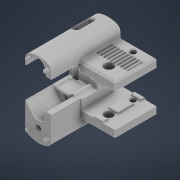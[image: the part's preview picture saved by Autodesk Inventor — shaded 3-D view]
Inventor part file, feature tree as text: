
AUTODESK INVENTOR PART (.ipt)
format: ipt  version: 2022.1 (Build 261234000, 234)  size: 1,613,312 bytes
history: native  units: mm
features: projected_geometry x40, extrude x31, sketch x31, reference x20, chamfer x19, other x11, move_body x11, direct_edit x8, fillet x7, hole x5, delete_face x5, plane x4, mirror x1
ambient origin geometry x8: Origin, YZ Plane, XZ Plane, XY Plane, X Axis, Y Axis, Z Axis, Center Point
bodies: Volumenkörper1 (feature_tree)
feature tree (193):
  extrude  "Extrusion1"  Depth=20.0mm
  extrude  "Extrusion2"  Depth=25.0mm
  plane  "Arbeitsebene1"
  extrude  "Extrusion5"  Depth=20.0mm
  sketch  "Skizze5"  dims[d7=20.0mm d8=10.0mm]
  extrude  "Extrusion6"  Depth=10.0mm
  hole  "Bohrung1"  [1 undecoded]
  extrude  "Extrusion10"  Depth=7.1mm
  sketch  "Skizze10"  dims[d28=15.0mm d29=17.0mm]
  hole  "Bohrung2"  [1 undecoded]
  hole  "Bohrung3"  [1 undecoded]
  extrude  "Extrusion11"  Depth=0.1mm
  extrude  "Extrusion12"  Depth=7.1mm
  direct_edit  "Direktbearbeitung3"
  direct_edit  "Direktbearbeitung4"
  extrude  "Extrusion13"  Depth=7.1mm
  fillet  "Rundung6"  Radius=18.2mm
  direct_edit  "Direktbearbeitung5"
  extrude  "Extrusion14"  Depth=11.0mm TaperAngle=0.0deg
  chamfer  "Fase2"  [1 undecoded]
  chamfer  "Fase3"  [1 undecoded]
  hole  "Bohrung5"  [1 undecoded]
  extrude  "Extrusion18"  Depth=4.0mm TaperAngle=0.0deg
  chamfer  "Fase4"  Distance=11.0mm
  extrude  "Extrusion19"  TaperAngle=0.0deg  [1 undecoded]
  chamfer  "Fase5"  Distance=1.2mm
  plane  "Arbeitsebene2"
  mirror  "Spiegeln1"
  extrude  "Extrusion20"  Depth=0.6mm
  fillet  "Rundung7"  Radius=1.2mm
  extrude  "Extrusion21"  Depth=0.6mm
  chamfer  "Fase6"  Distance=1.2mm
  extrude  "Extrusion22"  Depth=0.6mm
  chamfer  "Fase7"  Distance=6.2mm
  fillet  "Rundung8"  Radius=2.269mm
  chamfer  "Fase8"  Distance=10.561825mm
  chamfer  "Fase9"  Distance=10.561825mm
  extrude  "Extrusion23"  Depth=0.6mm
  extrude  "Extrusion24"  Depth=0.6mm
  direct_edit  "Direktbearbeitung6"
  direct_edit  "Direktbearbeitung7"
  chamfer  "Fase10"  Distance=0.8mm
  chamfer  "Fase11"  Distance=0.8mm
  fillet  "Rundung11"  Radius=0.8mm
  sketch  "Skizze27"  dims[d66=5.2mm d67=6.0mm d68=4.0mm d69=2.0mm d70=90.0deg d71=8.0mm d72=0.0mm]
  extrude  "Extrusion25"  Depth=0.6mm
  extrude  "Extrusion26"  Depth=0.6mm
  plane  "Arbeitsebene4"
  hole  "Bohrung6"  [1 undecoded]
  chamfer  "Fase12"  Distance=0.8mm
  direct_edit  "Direktbearbeitung8"
  plane  "Arbeitsebene3"
  extrude  "Extrusion27"  Depth=0.6mm
  extrude  "Extrusion28"  Depth=0.6mm
  chamfer  "Fase14"  Distance=8.638175mm
  chamfer  "Fase15"  Angle=90.0deg  [1 undecoded]
  chamfer  "Fase16"  Distance=1.0mm
  extrude  "Extrusion29"  Depth=1.0mm TaperAngle=45.0deg
  delete_face  "Fläche löschen1"
  extrude  "Extrusion30"  Depth=1.0mm TaperAngle=45.0deg
  fillet  "Rundung15"  Radius=3.95mm
  extrude  "Extrusion31"  Depth=0.6mm
  delete_face  "Fläche löschen2"
  extrude  "Extrusion32"  Depth=7.1mm
  fillet  "Rundung18"  Radius=1.975mm
  chamfer  "Fase19"  Distance=2.225mm
  chamfer  "Fase20"  [1 undecoded]
  sketch  "Skizze36"  dims[d110=1.2mm]
  extrude  "Extrusion33"  Depth=0.6mm
  extrude  "Extrusion34"  Depth=0.6mm
  extrude  "Extrusion35"  Depth=0.6mm
  delete_face  "Fläche löschen3"
  chamfer  "Fase23"  Distance=2.8mm
  chamfer  "Fase24"  Distance=2.2mm
  direct_edit  "Direktbearbeitung11"
  direct_edit  "Direktbearbeitung12"
  extrude  "Extrusion36"  Depth=0.6mm
  fillet  "Rundung20"  Radius=3.6mm
  sketch  "Skizze39"  dims[d112=1.2mm]
  delete_face  "Fläche löschen4"
  extrude  "Extrusion37"  Depth=0.6mm
  delete_face  "Fläche löschen5"
  extrude  "Extrusion38"  Depth=0.6mm
  chamfer  "Fase25"  Distance=4.95mm
  extrude  "Extrusion39"  Depth=0.5mm TaperAngle=45.0deg
  sketch  "Skizze1"  dims[d0=20.0mm d1=20.0mm]
  sketch  "Skizze2"  dims[d2=21.0mm d3=25.0mm]
  sketch  "Skizze4"  dims[d4=40.0mm d5=0.0mm d6=20.0mm]
  reference  "Referenz2"
  reference  "Referenz3"
  reference  "Referenz4"
  reference  "Referenz5"
  projected_geometry  "Projizierte Kontur2"
  sketch  "Skizze6"  dims[d9=0.0mm d10=0.0mm d11=-5.0mm]
  projected_geometry  "Projizierte Kontur3"
  sketch  "Skizze8"  dims[d25=7.1mm d26=7.1mm]
  reference  "Referenz6"
  reference  "Referenz7"
  projected_geometry  "Projizierte Kontur6"
  projected_geometry  "Projizierte Kontur7"
  reference  "Referenz9"
  sketch  "Skizze11"  dims[d30=1.0mm d31=18.0mm]
  projected_geometry  "Projizierte Kontur8"
  projected_geometry  "Projizierte Kontur9"
  sketch  "Skizze12"  dims[d32=18.2mm d33=0.1mm]
  projected_geometry  "Projizierte Kontur10"
  projected_geometry  "Projizierte Kontur11"
  sketch  "Skizze13"  dims[d34=36.0mm d35=0.0mm d36=7.1mm]
  projected_geometry  "Projizierte Kontur12"
  sketch  "Skizze14"  dims[d37=3.55mm d39=7.1mm d40=18.2mm]
  projected_geometry  "Projizierte Kontur13"
  projected_geometry  "Projizierte Kontur17"
  projected_geometry  "Projizierte Kontur18"
  sketch  "Skizze20"  dims[d41=9.1mm d42=11.0mm d43=0.0mm]
  projected_geometry  "Projizierte Kontur19"
  sketch  "Skizze21"  dims[d48=3.4mm d49=6.0mm d50=4.0mm d51=2.0mm d52=90.0deg d53=8.0mm d54=0.0mm d59=0.0mm d60=0.0mm]
  projected_geometry  "Projizierte Kontur20"
  sketch  "Skizze22"  dims[d61=40.0mm]
  projected_geometry  "Projizierte Kontur21"
  sketch  "Skizze23"  dims[d62=15.5mm]
  projected_geometry  "Projizierte Kontur22"
  sketch  "Skizze24"  dims[d63=10.0mm]
  projected_geometry  "Projizierte Kontur23"
  sketch  "Skizze25"  dims[d64=6.2385mm]
  reference  "Referenz12"
  reference  "Referenz13"
  reference  "Referenz14"
  reference  "Referenz15"
  sketch  "Skizze26"  dims[d65=14.53mm]
  projected_geometry  "Projizierte Kontur24"
  projected_geometry  "Projizierte Kontur25"
  projected_geometry  "Projizierte Kontur26"
  projected_geometry  "Projizierte Kontur27"
  projected_geometry  "Projizierte Kontur28"
  sketch  "Skizze28"  dims[d73=3.2mm d74=6.0mm d75=4.0mm d76=2.0mm d77=90.0deg d78=8.0mm d79=0.0mm d80=0.0mm d81=0.0mm]
  sketch  "Skizze29"  dims[d82=11.0mm d83=0.0mm d87=0.0mm d88=0.0mm d89=4.0mm]
  projected_geometry  "Projizierte Kontur29"
  sketch  "Skizze30"  dims[d90=0.0mm d91=0.0mm d92=4.0mm d93=0.0mm d94=0.0mm d95=4.0mm]
  projected_geometry  "Projizierte Kontur30"
  projected_geometry  "Projizierte Kontur31"
  reference  "Referenz18"
  sketch  "Skizze31"  dims[d101=40.0mm]
  projected_geometry  "Projizierte Kontur32"
  projected_geometry  "Projizierte Kontur33"
  projected_geometry  "Projizierte Kontur34"
  sketch  "Skizze32"  dims[d102=20.0mm d103=11.0mm d104=0.0mm]
  projected_geometry  "Projizierte Kontur35"
  sketch  "Skizze33"  dims[d105=4.0mm d106=0.0mm d107=0.0mm d108=-5.0mm]
  projected_geometry  "Projizierte Kontur36"
  projected_geometry  "Projizierte Kontur37"
  sketch  "Skizze34"  dims[d109=9.4mm]
  projected_geometry  "Projizierte Kontur38"
  projected_geometry  "Projizierte Kontur39"
  reference  "Referenz20"
  projected_geometry  "Projizierte Kontur40"
  projected_geometry  "Projizierte Kontur41"
  sketch  "Skizze37"  dims[d111=1.2mm]
  reference  "Referenz21"
  reference  "Referenz22"
  reference  "Referenz23"
  reference  "Referenz24"
  reference  "Referenz25"
  reference  "Referenz26"
  reference  "Referenz27"
  sketch  "Skizze40"  dims[d113=1.2mm]
  projected_geometry  "Projizierte Kontur42"
  projected_geometry  "Projizierte Kontur43"
  projected_geometry  "Projizierte Kontur44"
  projected_geometry  "Projizierte Kontur45"
  projected_geometry  "Projizierte Kontur46"
  sketch  "Skizze41"  dims[d114=1.2mm d115=1.2mm d116=1.2mm d117=1.2mm d118=1.2mm d119=1.2mm d121=6.2mm d122=6.2mm d123=2.269mm d124=10.561825mm d125=10.561825mm d126=0.8mm d127=0.8mm d128=0.8mm d129=0.8mm d130=0.8mm d131=0.8mm d132=0.8mm d133=0.8mm d134=0.8mm d135=14.53mm d136=6.2385mm d137=8.638175mm d138=90.0deg d139=1.0mm d140=0.0mm d141=1.0mm d142=2.0mm d143=45.0deg d146=1.0mm d147=2.0mm d148=45.0deg d160=3.95mm d161=4.45mm d162=7.1mm d163=1.975mm d164=2.225mm d165=0.0mm d166=3.55mm d169=2.8mm d170=2.8mm d171=2.8mm d172=2.2mm d173=2.8mm d174=6.0mm d175=3.05mm d176=2.0mm d177=8.726646mm d178=7.2mm d179=0.0mm d180=2.0mm d181=3.6mm d182=2.0mm d183=3.6mm d184=4.95mm d185=0.0mm d186=0.5mm d187=2.0mm d188=45.0deg d189=5.8mm d190=25.0mm d191=12.5mm d192=0.0mm d193=1.0mm d194=0.0mm d195=1.0mm d196=2.0mm d197=45.0deg d198=5.0mm d199=0.0mm d200=0.0mm d201=1.0mm d202=1.0mm d203=0.0mm d204=1.0mm d205=2.0mm d206=45.0deg d207=135.0deg d208=0.0mm d209=0.0mm d210=1.0mm d211=2.0mm d212=45.0deg d213=5.0mm d214=1.0mm d215=2.0mm d216=45.0deg d217=0.7071mm d218=2.0mm d219=45.0deg d220=4.0mm d221=11.1mm d222=1.38mm d223=9.0mm d224=1.31mm d225=1.31mm d226=1.05mm d227=1.648525mm d228=1.0mm d229=0.0mm d230=0.0mm d231=6.5mm d232=0.0mm d233=0.0mm d234=0.0mm d235=1.0mm d236=0.0mm d237=0.0mm d238=6.0mm d239=0.6mm d240=2.0mm d241=45.0deg d242=0.6mm d243=2.0mm d244=45.0deg d247=0.5mm d248=0.01mm d249=0.01mm d250=0.07mm d251=0.07mm d252=0.1mm d253=0.1mm d254=10.0mm d255=0.0mm d256=10.0mm d257=0.0mm d259=3.3mm d260=6.0mm d261=6.5mm d262=3.4mm d263=90.0deg d264=10.1mm d265=0.0mm d266=0.4mm d267=2.0mm d268=45.0deg d269=0.0mm d270=0.0mm d271=0.5mm d273=7.24mm d274=5.8mm d275=0.72mm d276=6.8mm d279=1.0mm d280=5.8mm d281=2.0mm d282=19.02mm d283=0.0mm d288=5.0mm d289=0.0mm d290=0.0mm d291=1.0mm d292=2.0mm d293=45.0deg d294=1.0mm d295=2.0mm d296=45.0deg d297=3.0mm d298=2.0mm d299=45.0deg d300=9.71mm d301=0.0mm d302=0.0mm d303=0.0mm d304=1.0mm d305=2.0mm d306=0.0mm d315=2.0mm d316=2.0mm d317=2.0mm d318=0.0mm d319=0.4mm d339=0.4mm d340=2.0mm d341=45.0deg d342=0.4mm d343=2.0mm d344=45.0deg d345=8.6mm d346=0.1mm d348=0.1mm d349=0.1mm d350=0.1mm d351=0.1mm d352=24.0mm d353=12.0mm d354=4.2mm d355=0.0mm d356=0.0mm d357=10.0mm d358=0.0mm d359=1.8mm d360=10.0mm d361=0.0mm d368=0.4mm d369=2.0mm d370=45.0deg d371=0.4mm d372=2.0mm d373=45.0deg d374=0.0mm d375=0.0mm d376=-3.0mm d377=0.0mm d378=0.0mm d379=-3.0mm d380=0.0mm d381=0.0mm d382=-1.5mm d383=0.0mm d384=0.0mm d385=-2.5mm d386=4.7mm d387=3.828427mm d388=2.3mm d389=2.0mm d390=2.0mm d391=0.0mm d392=2.38mm d393=2.38mm d394=0.0mm d395=2.5mm d396=8.48mm d401=0.04mm d402=0.04mm d403=0.04mm d404=0.04mm d405=0.04mm d406=0.04mm d408=10.0mm d409=0.0mm d410=3.0mm d429=0.0mm d430=2.861mm d439=90.0deg d440=90.0deg d441=2.722015mm d442=2.721996mm d443=2.51674mm d444=6.217998mm d445=10.025268mm d446=10.017026mm d447=10.036881mm d448=2.721987mm d449=2.721987mm d450=16.502008mm d451=26.892014mm d452=19.554014mm d453=5.384897mm d454=5.383896mm d455=3.419227mm d456=0.41494mm d457=0.008242mm d458=10.0mm d459=0.0mm d460=0.106442mm d461=1.0mm d462=0.106442mm d463=0.11295mm d464=0.11295mm d465=10.0mm d466=0.0mm d467=1.0mm d468=2.0mm d469=45.0deg d470=15.5mm d471=1.0mm d472=8.5mm d473=8.0mm d474=12.0mm d475=2.5mm d476=0.6mm d477=0.0mm]
  other  "<userpath>\Desktop\Voron-2-2.4r1\Custom\Front_Idlers\Baugruppe1.iam"
  other  "Baugruppe1.iam"
  other  "Inside-holder:1"
  move_body  "Verschieben3"
  move_body  "Verschieben4"
  move_body  "Verschieben5"
  move_body  "Verschieben6"
  other  "<userpath>\Desktop\Voron-2-2.4r1\CAD\VORON2_v2.4_Assembly_Step\VORON2 v2.4 Assembly.iam"
  other  "VORON2 v2.4 Assembly.iam"
  other  "Z Assembly:1"
  other  "Z Belts:1"
  other  "Z Belt:2"
  move_body  "Verschieben7"
  move_body  "Verschieben8"
  move_body  "Verschieben9"
  other  "<userpath>\Desktop\Voron-2-2.4r1\Custom\Front_Idlers\Assembly_Front-Idlers2.iam"
  other  "Assembly_Front-Idlers2.iam"
  other  "Cover1:1"
  move_body  "Verschieben16"
  move_body  "Verschieben17"
  move_body  "Verschieben18"
  move_body  "Verschieben19"
note: 10 required parameter values undecoded (feature->parameter linkage not recoverable at this tier; creation-order binding heuristic only, values carry confidence <= 0.55)
